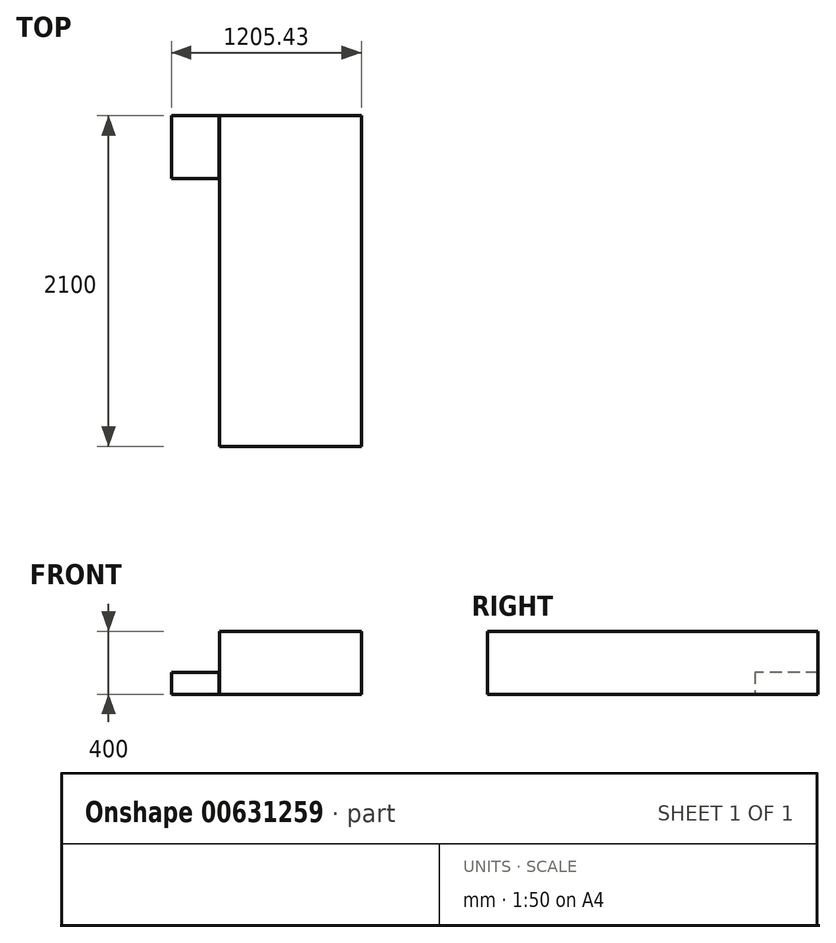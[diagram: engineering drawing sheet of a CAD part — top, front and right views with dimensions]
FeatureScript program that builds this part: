
annotation { "Feature Type Name" : "Feature", "Feature Type Description" : "" }
export const myFeature = defineFeature(function(context is Context, id is Id, definition is map)
    precondition{}
    {
        {
            var Q0;
            Q0=qCreatedBy(makeId("Top.planeOp"),FACE);
            var sketch = newSketch(context, id + "F0", { "sketchPlane" : qUnion([Q0])});
            skLineSegment(sketch, "E0.bottom", {"start": v(0, 2100) * mm, "end": v(-900, 2100) * mm});
            skLineSegment(sketch, "E0.top", {"start": v(0, 0) * mm, "end": v(-900, 0) * mm});
            skLineSegment(sketch, "E0.left", {"start": v(0, 2100) * mm, "end": v(0, 0) * mm});
            skLineSegment(sketch, "E0.right", {"start": v(-900, 2100) * mm, "end": v(-900, 0) * mm});
            skSolve(sketch);
        }
        {
            var Q0;
            Q0=makeQuery(id+"F0.imprint","IMPRINT",FACE,{"disambiguationData":[TD([[makeQuery(id+"F0.imprint","IMPRINT",EDGE,{"derivedFrom":sQuery(id+"F0.wireOp",EDGE,"E0.bottom")}),1.0]])]});
            var sketch = newSketch(context, id + "F1", { "sketchPlane" : qUnion([Q0])});
            skLineSegment(sketch, "E1.bottom", {"start": v(-1205.43, 2099.46) * mm, "end": v(-905.43, 2099.46) * mm});
            skLineSegment(sketch, "E1.top", {"start": v(-1205.43, 1699.46) * mm, "end": v(-905.43, 1699.46) * mm});
            skLineSegment(sketch, "E1.left", {"start": v(-1205.43, 2099.46) * mm, "end": v(-1205.43, 1699.46) * mm});
            skLineSegment(sketch, "E1.right", {"start": v(-905.43, 2099.46) * mm, "end": v(-905.43, 1699.46) * mm});
            skLineSegment(sketch, "E2.left", {"start": v(-1205.43, 2099.46) * mm, "end": v(-1205.43, 2099.46) * mm});
            skLineSegment(sketch, "E2.right", {"start": v(-905.43, 2099.46) * mm, "end": v(-905.43, 2099.46) * mm});
            skSolve(sketch);
        }
        {
            var Q0;
            Q0 = qSketchRegion(id + "F0", true);
            extrude(context, id + "F2", {"entities" : qUnion([Q0]), "depth" : 400 * mm, "offsetDistance" : 25 * mm});
        }
        {
            var Q0;
            Q0 = qSketchRegion(id + "F1", true);
            extrude(context, id + "F3", {"entities" : qUnion([Q0]), "depth" : 140 * mm, "offsetDistance" : 25 * mm});
        }
    });
